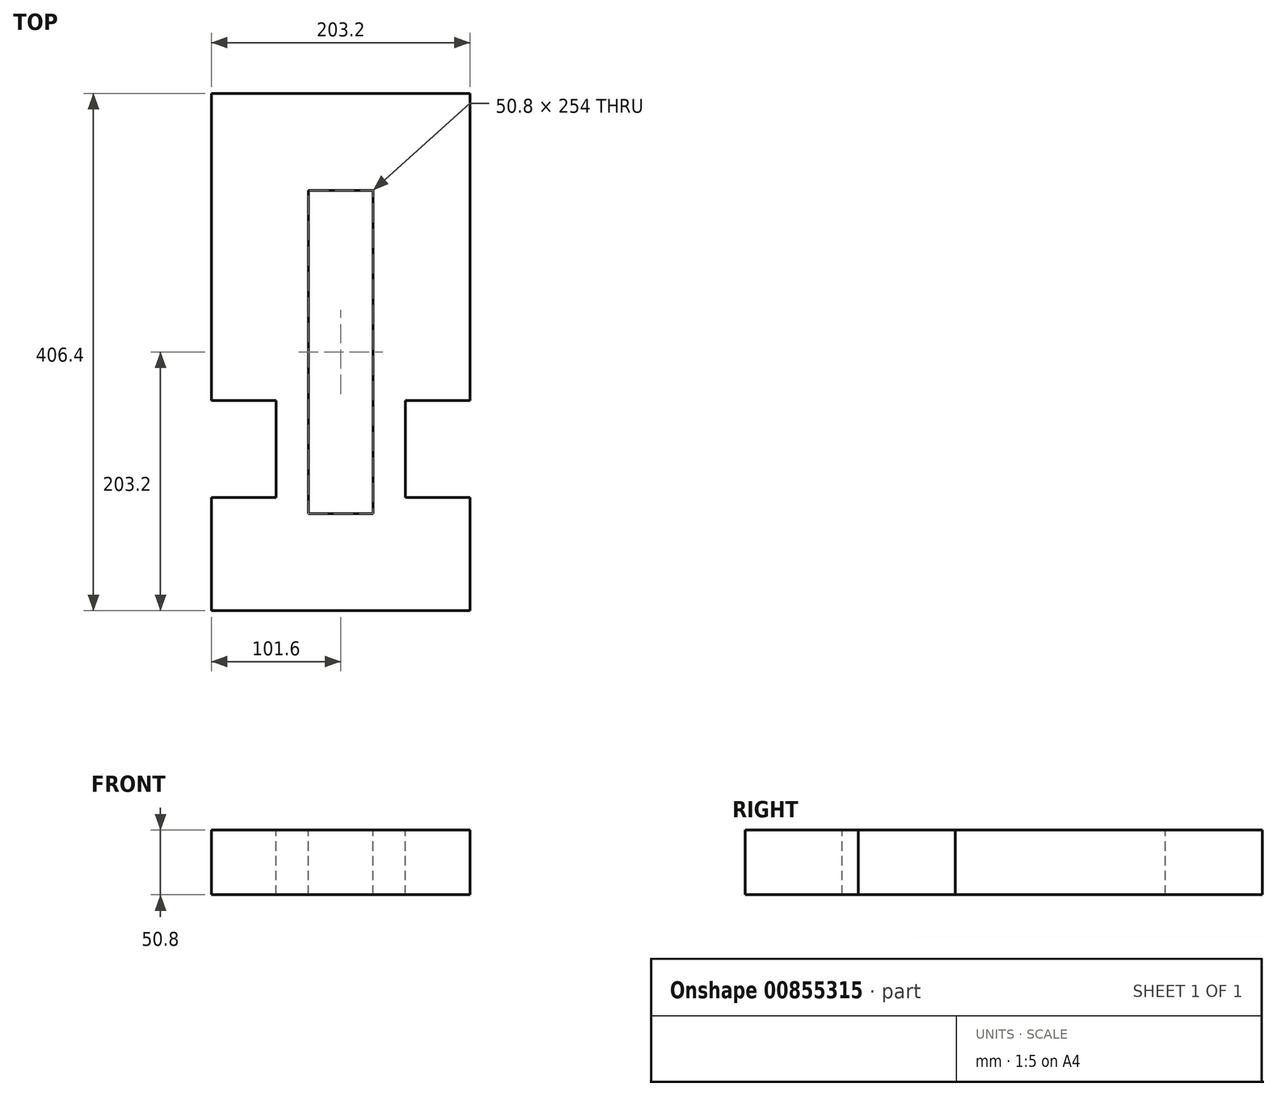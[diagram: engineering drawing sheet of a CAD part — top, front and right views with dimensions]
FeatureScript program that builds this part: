
annotation { "Feature Type Name" : "Feature", "Feature Type Description" : "" }
export const myFeature = defineFeature(function(context is Context, id is Id, definition is map)
    precondition{}
    {
        {
            var Q0;
            Q0=qCreatedBy(makeId("Top.planeOp"),FACE);
            var sketch = newSketch(context, id + "F0", { "sketchPlane" : qUnion([Q0])});
            skLineSegment(sketch, "E0.bottom", {"start": v(101.6, -203.2) * mm, "end": v(-101.6, -203.2) * mm});
            skLineSegment(sketch, "E0.top", {"start": v(101.6, 203.2) * mm, "end": v(-101.6, 203.2) * mm});
            skLineSegment(sketch, "E0.left", {"start": v(101.6, -203.2) * mm, "end": v(101.6, 203.2) * mm});
            skLineSegment(sketch, "E0.right", {"start": v(-101.6, -203.2) * mm, "end": v(-101.6, 203.2) * mm});
            skPoint(sketch, "E0.middle", {"position": v(0, 0) * mm});
            skSolve(sketch);
        }
        {
            var Q0;
            Q0 = qSketchRegion(id + "F0", true);
            extrude(context, id + "F1", {"entities" : qUnion([Q0]), "depth" : 50.8 * mm, "offsetDistance" : 25 * mm});
        }
        {
            var Q0;
            Q0=makeQuery(id+"F1.opExtrude","CAP_FACE",FACE,{"disambiguationData":[OSD([sQuery(id+"F0.wireOp",EDGE,"E0.bottom"),sQuery(id+"F0.wireOp",EDGE,"E0.top"),sQuery(id+"F0.wireOp",EDGE,"E0.left"),sQuery(id+"F0.wireOp",EDGE,"E0.right")])],"isStart":false});
            var sketch = newSketch(context, id + "F2", { "sketchPlane" : qUnion([Q0])});
            skLineSegment(sketch, "E1.bottom", {"start": v(25.4, -127) * mm, "end": v(-25.4, -127) * mm});
            skLineSegment(sketch, "E1.top", {"start": v(25.4, 127) * mm, "end": v(-25.4, 127) * mm});
            skLineSegment(sketch, "E1.left", {"start": v(25.4, -127) * mm, "end": v(25.4, 127) * mm});
            skLineSegment(sketch, "E1.right", {"start": v(-25.4, -127) * mm, "end": v(-25.4, 127) * mm});
            skPoint(sketch, "E1.middle", {"position": v(0, 0) * mm});
            skLineSegment(sketch, "E2.bottom", {"start": v(-50.8, -38.1) * mm, "end": v(-101.6, -38.1) * mm});
            skLineSegment(sketch, "E2.top", {"start": v(-50.8, -114.3) * mm, "end": v(-101.6, -114.3) * mm});
            skLineSegment(sketch, "E2.left", {"start": v(-50.8, -38.1) * mm, "end": v(-50.8, -114.3) * mm});
            skLineSegment(sketch, "E2.right", {"start": v(-101.6, -38.1) * mm, "end": v(-101.6, -114.3) * mm});
            skPoint(sketch, "E3", {"position": v(-101.6, -76.2) * mm});
            skLineSegment(sketch, "E4.bottom", {"start": v(101.6, -114.3) * mm, "end": v(50.8, -114.3) * mm});
            skLineSegment(sketch, "E4.top", {"start": v(101.6, -38.1) * mm, "end": v(50.8, -38.1) * mm});
            skLineSegment(sketch, "E4.left", {"start": v(101.6, -114.3) * mm, "end": v(101.6, -38.1) * mm});
            skLineSegment(sketch, "E4.right", {"start": v(50.8, -114.3) * mm, "end": v(50.8, -38.1) * mm});
            skPoint(sketch, "E4.middle", {"position": v(76.2, -76.2) * mm});
            skSolve(sketch);
        }
        {
            var Q0;
            Q0 = qSketchRegion(id + "F2", true);
            extrude(context, id + "F3", {"entities" : qUnion([Q0]), "operationType" : NewBodyOperationType.REMOVE, "endBound" : BoundingType.THROUGH_ALL, "oppositeDirection" : true, "depth" : 25 * mm, "offsetDistance" : 25 * mm});
        }
    });
